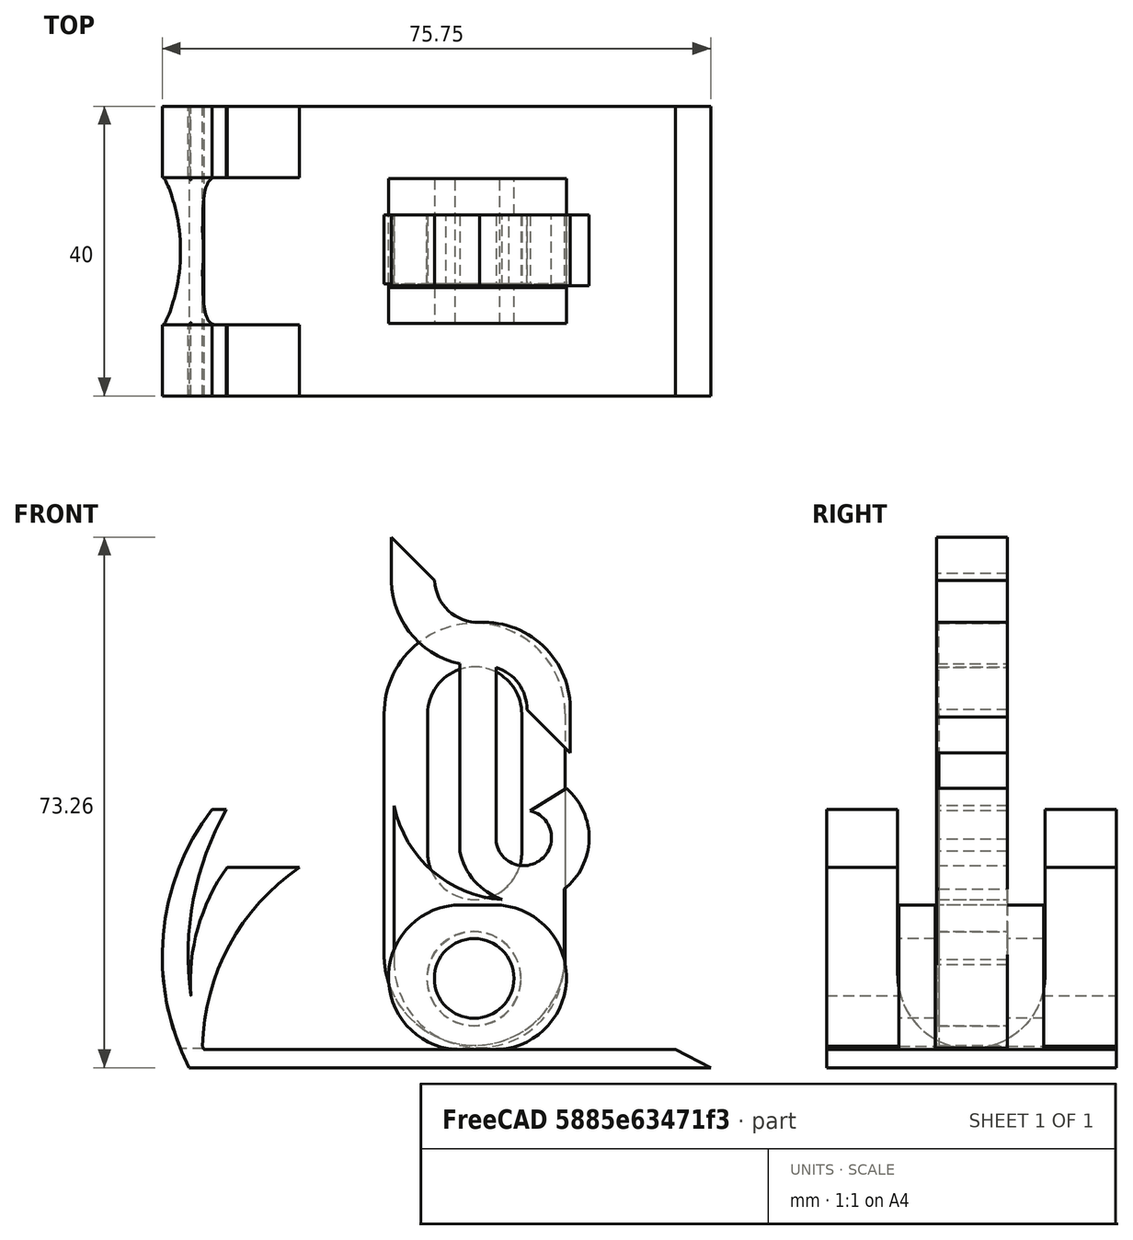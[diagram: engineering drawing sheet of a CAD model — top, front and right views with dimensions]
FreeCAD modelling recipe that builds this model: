
FCSTD DOCUMENT  (FreeCAD 0.16R6712 (Git))
Label: support_telephone4
License: All rights reserved
LicenseURL: http://en.wikipedia.org/wiki/All_rights_reserved
objects: Sketcher::SketchObject×10, PartDesign::Pad×9, App::DocumentObjectGroup×4, Part::Cut×2, Part::MultiFuse×2, PartDesign::Pocket×1, Mesh::Feature×1
note: 34 computed .brp shape members not serialized (recipe doc carries the construction recipe); baked Part::Feature solids carry a one-line shape summary decoded from their .brp

FEATURE [Sketcher::SketchObject] Sketch
  Placement = pos=(0,20,0) rot=(1,0,0;1.5708rad)
  sketch-geometry (10):
    g0: LineSegment StartX=-4.14304 StartY=-1.67863 StartZ=0 EndX=67.8914 EndY=-1.67863 EndZ=0
    g1: LineSegment StartX=-2.14304 StartY=0.821368 StartZ=0 EndX=63.0091 EndY=0.821368 EndZ=0
    g2: LineSegment StartX=63.0091 StartY=0.821368 StartZ=0 EndX=67.8914 EndY=-1.67863 EndZ=0
    g3: GeomPoint [constr] X=-1 Y=34 Z=0
    g4: GeomPoint [constr] X=1 Y=34 Z=0
    g5: ArcOfCircle CenterX=25.6862 CenterY=13.6714 CenterZ=0 NormalX=0 NormalY=0 NormalZ=1 Radius=33.5471 StartAngle=2.4906 EndAngle=3.61685
    g6: ArcOfCircle CenterX=36.4379 CenterY=13.9048 CenterZ=0 NormalX=0 NormalY=0 NormalZ=1 Radius=40.739 StartAngle=2.62575 EndAngle=3.46854
    g7: LineSegment StartX=-1 StartY=34 StartZ=0 EndX=1 EndY=34 EndZ=0
    g8: GeomPoint [constr] X=11 Y=26 Z=0
    g9: GeomPoint [constr] X=1.03178 Y=26 Z=0
  constraints (19):
    c: Horizontal(g0)
    c: Horizontal(g1)
    c: DistanceX(g0,g1) = 2
    c: Coincident(g2,g1)
    c: Coincident(g2,g0)
    c: DistanceX(g3,g-1) = 1
    c: DistanceY(g-1,g4) = 34
    c: DistanceY(g-1,g3) = 34
    c: DistanceX(g-1,g4) = 1
    c: Coincident(g5,g3)
    c: Coincident(g5,g0)
    c: Coincident(g6,g4)
    c: Coincident(g6,g1)
    c: Coincident(g7,g3)
    c: Coincident(g7,g4)
    c: DistanceY(g8,g4) = 8
    c: DistanceX(g4,g8) = 10
    c: DistanceY(g0,g1) = 2.5
    c: DistanceY(g-1,g1) = 0.821368
FEATURE [PartDesign::Pad] Pad
  Length = 40
  Length2 = 100
  Placement = pos=(0,20,0) rot=(1,0,0;1.5708rad)
  Sketch = -> Sketch
  Type = 0
FEATURE [Sketcher::SketchObject] Sketch001
  Placement = pos=(10,10,0) rot=(1,0,0;1.5708rad)
  sketch-geometry (4):
    g0: ArcOfCircle CenterX=23.3752 CenterY=10.7904 CenterZ=0 NormalX=0 NormalY=0 NormalZ=1 Radius=10 StartAngle=1.5708 EndAngle=4.71239
    g1: ArcOfCircle CenterX=27.9635 CenterY=10.7904 CenterZ=0 NormalX=0 NormalY=0 NormalZ=1 Radius=10 StartAngle=4.71239 EndAngle=7.85398
    g2: LineSegment StartX=23.3752 StartY=0.790424 StartZ=0 EndX=27.9635 EndY=0.790424 EndZ=0
    g3: LineSegment StartX=23.3752 StartY=20.7904 StartZ=0 EndX=27.9635 EndY=20.7904 EndZ=0
  constraints (7):
    c: Tangent(g0,g3) = 1.5708
    c: Tangent(g0,g2) = -1.5708
    c: Tangent(g2,g1) = -1.5708
    c: Tangent(g3,g1) = 1.5708
    c: Horizontal(g2)
    c: Equal(g0,g1)
    c: DistanceY(g1,g1) = 20
FEATURE [PartDesign::Pad] Pad001
  Length = 20
  Length2 = 100
  Placement = pos=(10,10,0) rot=(1,0,0;1.5708rad)
  Sketch = -> Sketch001
  Type = 0
FEATURE [Sketcher::SketchObject] Sketch002
  Placement = pos=(10,-10,0) rot=(1,0,0;1.5708rad)
  Support = -> Pad001 [Face6]
  sketch-geometry (1):
    g0: Circle CenterX=25.215 CenterY=10.6479 CenterZ=0 NormalX=0 NormalY=0 NormalZ=1 Radius=5.5
  constraints (1):
    c: Radius(g0) = 5.5
FEATURE [PartDesign::Pocket] Pocket
  Length = 24
  Placement = pos=(10,10,0) rot=(1,0,0;1.5708rad)
  Sketch = -> Sketch002
  Type = 0
FEATURE [Sketcher::SketchObject] Sketch003
  Placement = pos=(10,0,1) rot=(0,0,1;0rad)
  sketch-geometry (4):
    g0: LineSegment StartX=13.2912 StartY=5 StartZ=0 EndX=37.9673 EndY=5 EndZ=0
    g1: LineSegment StartX=37.9673 StartY=5 StartZ=0 EndX=37.9673 EndY=-5 EndZ=0
    g2: LineSegment StartX=37.9673 StartY=-5 StartZ=0 EndX=13.2912 EndY=-5 EndZ=0
    g3: LineSegment StartX=13.2912 StartY=-5 StartZ=0 EndX=13.2912 EndY=5 EndZ=0
  constraints (10):
    c: Coincident(g0,g1)
    c: Coincident(g1,g2)
    c: Coincident(g2,g3)
    c: Coincident(g3,g0)
    c: Horizontal(g0)
    c: Horizontal(g2)
    c: Vertical(g1)
    c: Vertical(g3)
    c: Symmetric(g0,g1,g-1)
    c: DistanceY(g1,g1) = 10
FEATURE [PartDesign::Pad] Pad002
  Length = 25
  Length2 = 100
  Placement = pos=(10,0,1) rot=(0,0,1;0rad)
  Sketch = -> Sketch003
  Type = 0
FEATURE [Part::Cut] Cut
  Base = -> Pocket
  Tool = -> Pad002
FEATURE [Sketcher::SketchObject] Sketch004
  Placement = pos=(10,5,0) rot=(1,0,0;1.5708rad)
  sketch-geometry (9):
    g0: ArcOfCircle CenterX=25.292 CenterY=47.1685 CenterZ=0 NormalX=0 NormalY=0 NormalZ=1 Radius=12.5141 StartAngle=0 EndAngle=3.14159
    g1: ArcOfCircle CenterX=25.292 CenterY=13.9216 CenterZ=0 NormalX=0 NormalY=0 NormalZ=1 Radius=12.5141 StartAngle=3.14159 EndAngle=6.28319
    g2: LineSegment StartX=12.7779 StartY=47.1685 StartZ=0 EndX=12.7779 EndY=13.9216 EndZ=0
    g3: LineSegment StartX=37.8061 StartY=47.1685 StartZ=0 EndX=37.8061 EndY=13.9216 EndZ=0
    g4: Circle CenterX=25.2029 CenterY=10.5785 CenterZ=0 NormalX=0 NormalY=0 NormalZ=1 Radius=6.5
    g5: ArcOfCircle CenterX=25.292 CenterY=47.1685 CenterZ=0 NormalX=0 NormalY=0 NormalZ=1 Radius=6.5 StartAngle=0 EndAngle=3.14159
    g6: ArcOfCircle CenterX=25.292 CenterY=28.0341 CenterZ=0 NormalX=0 NormalY=0 NormalZ=1 Radius=6.5 StartAngle=3.14159 EndAngle=6.28319
    g7: LineSegment StartX=18.792 StartY=47.1685 StartZ=0 EndX=18.792 EndY=28.0341 EndZ=0
    g8: LineSegment StartX=31.792 StartY=47.1685 StartZ=0 EndX=31.792 EndY=28.0341 EndZ=0
  constraints (15):
    c: Tangent(g0,g3) = 1.5708
    c: Tangent(g0,g2) = -1.5708
    c: Tangent(g2,g1) = -1.5708
    c: Tangent(g3,g1) = 1.5708
    c: Vertical(g2)
    c: Equal(g0,g1)
    c: Radius(g4) = 6.5
    c: Tangent(g5,g8) = 1.5708
    c: Tangent(g5,g7) = -1.5708
    c: Tangent(g7,g6) = -1.5708
    c: Tangent(g8,g6) = 1.5708
    c: Vertical(g7)
    c: Equal(g5,g6)
    c: Coincident(g5,g0)
    c: DistanceX(g5,g5) = 13
FEATURE [PartDesign::Pad] Pad003
  Length = 9.5
  Length2 = 100
  Placement = pos=(10,5,0) rot=(1,0,0;1.5708rad)
  Sketch = -> Sketch004
  Type = 0
FEATURE [App::DocumentObjectGroup] Groupe001  label="bielle"
  Group = -> [Pad003]
FEATURE [Sketcher::SketchObject] Sketch005
  Placement = pos=(0,5,0) rot=(1,0,0;1.5708rad)
  sketch-geometry (9):
    g0: ArcOfCircle CenterX=36.5044 CenterY=47.8329 CenterZ=0 NormalX=0 NormalY=0 NormalZ=1 Radius=6 StartAngle=6.27141 EndAngle=7.90556
    g1: ArcOfCircle CenterX=36.5044 CenterY=47.8329 CenterZ=0 NormalX=0 NormalY=0 NormalZ=1 Radius=12 StartAngle=6.19385 EndAngle=7.90026
    g2: ArcOfCircle CenterX=35.7669 CenterY=65.8173 CenterZ=0 NormalX=0 NormalY=0 NormalZ=1 Radius=6 StartAngle=3.18098 EndAngle=4.74278
    g3: ArcOfCircle CenterX=35.7669 CenterY=65.8173 CenterZ=0 NormalX=0 NormalY=0 NormalZ=1 Radius=12 StartAngle=3.0779 EndAngle=4.74808
    g4: GeomPoint [constr] X=35.7418 Y=56.8329 Z=0
    g5: LineSegment StartX=48.4566 StartY=46.7623 StartZ=0 EndX=48.4566 EndY=41.7623 EndZ=0
    g6: LineSegment StartX=42.504 StartY=47.7623 StartZ=0 EndX=48.4566 EndY=41.7623 EndZ=0
    g7: LineSegment StartX=23.7913 StartY=66.581 StartZ=0 EndX=23.7913 EndY=71.581 EndZ=0
    g8: LineSegment StartX=23.7913 StartY=71.581 StartZ=0 EndX=29.7716 EndY=65.581 EndZ=0
  constraints (23):
    c: Coincident(g1,g0)
    c: Radius(g1) = 12
    c: Radius(g0) = 6
    c: Coincident(g2,g1)
    c: Coincident(g3,g2)
    c: Coincident(g3,g0)
    c: Radius(g2) = 6
    c: Radius(g3) = 12
    c: DistanceX(g-1,g4) = 35.7418
    c: DistanceY(g-1,g4) = 56.8329
    c: DistanceY(g0,g4) = 9
    c: Coincident(g5,g1)
    c: Vertical(g5)
    c: Coincident(g6,g0)
    c: Coincident(g6,g5)
    c: DistanceY(g5,g5) = 5
    c: Coincident(g7,g3)
    c: Vertical(g7)
    c: Coincident(g8,g7)
    c: Coincident(g8,g2)
    c: DistanceY(g7,g7) = 5
    c: DistanceY(g2,g7) = 6
    c: DistanceY(g5,g0) = 6
FEATURE [Sketcher::SketchObject] Sketch006
  Placement = pos=(0,5,0) rot=(1,0,0;1.5708rad)
  sketch-geometry (6):
    g0: LineSegment StartX=33.2207 StartY=59.5118 StartZ=0 EndX=33.2207 EndY=28.1907 EndZ=0
    g1: LineSegment StartX=38.2207 StartY=59.3183 StartZ=0 EndX=38.2207 EndY=29.8591 EndZ=0
    g2: ArcOfCircle CenterX=42.054 CenterY=30.0624 CenterZ=0 NormalX=0 NormalY=0 NormalZ=1 Radius=9.02936 StartAngle=3.3504 EndAngle=7.14053
    g3: ArcOfCircle CenterX=42.054 CenterY=30.0624 CenterZ=0 NormalX=0 NormalY=0 NormalZ=1 Radius=3.83862 StartAngle=3.19457 EndAngle=7.61485
    g4: LineSegment StartX=42.9632 StartY=33.7918 StartZ=0 EndX=47.9632 EndY=36.8896 EndZ=0
    g5: LineSegment StartX=33.2207 StartY=59.5118 StartZ=0 EndX=38.2207 EndY=59.3183 EndZ=0
  constraints (11):
    c: Vertical(g0)
    c: Vertical(g1)
    c: DistanceX(g0,g1) = 5
    c: Coincident(g2,g0)
    c: Coincident(g3,g2)
    c: Coincident(g3,g1)
    c: Coincident(g4,g3)
    c: Coincident(g4,g2)
    c: DistanceX(g3,g2) = 5
    c: Coincident(g5,g0)
    c: Coincident(g5,g1)
FEATURE [Sketcher::SketchObject] Sketch007
  Placement = pos=(0,5,0) rot=(1,0,0;1.5708rad)
  sketch-geometry (5):
    g0: Circle CenterX=35.1655 CenterY=10.6403 CenterZ=0 NormalX=0 NormalY=0 NormalZ=1 Radius=6.5
    g1: ArcOfCircle CenterX=35.9044 CenterY=12.8543 CenterZ=0 NormalX=0 NormalY=0 NormalZ=1 Radius=11.7583 StartAngle=3.10975 EndAngle=6.25328
    g2: LineSegment StartX=47.6574 StartY=12.5027 StartZ=0 EndX=47.6574 EndY=23.355 EndZ=0
    g3: LineSegment StartX=24.1521 StartY=34.4704 StartZ=0 EndX=24.1521 EndY=13.2287 EndZ=0
    g4: ArcOfCircle CenterX=40.1211 CenterY=37.8289 CenterZ=0 NormalX=0 NormalY=0 NormalZ=1 Radius=16.3184 StartAngle=3.34889 EndAngle=5.19244
  constraints (7):
    c: Radius(g0) = 6.5
    c: Coincident(g2,g1)
    c: Vertical(g2)
    c: Coincident(g3,g1)
    c: Vertical(g3)
    c: Coincident(g4,g3)
    c: Coincident(g4,g2)
FEATURE [PartDesign::Pad] Pad004
  Length = 9.8
  Length2 = 100
  Placement = pos=(0,5,0) rot=(1,0,0;1.5708rad)
  Sketch = -> Sketch006
  Type = 0
FEATURE [PartDesign::Pad] Pad005
  Length = 9.8
  Length2 = 100
  Placement = pos=(0,5,0) rot=(1,0,0;1.5708rad)
  Sketch = -> Sketch005
  Type = 0
FEATURE [PartDesign::Pad] Pad006
  Length = 9.8
  Length2 = 100
  Placement = pos=(0,5,0) rot=(1,0,0;1.5708rad)
  Sketch = -> Sketch007
  Type = 0
FEATURE [Part::MultiFuse] Fusion
  Shapes = -> [Pad004,Pad005,Pad006]
FEATURE [App::DocumentObjectGroup] Groupe002  label="bielle_J"
  Group = -> [Fusion]
FEATURE [Sketcher::SketchObject] Sketch008
  Placement = pos=(0,20,0) rot=(1,0,0;1.5708rad)
  sketch-geometry (6):
    g0: GeomPoint [constr] X=11.0569 Y=25.9534 Z=0
    g1: GeomPoint [constr] X=1.09392 Y=25.9534 Z=0
    g2: GeomPoint [constr] X=-2.3075 Y=0.868989 Z=0
    g3: ArcOfCircle CenterX=28.3339 CenterY=0.646249 CenterZ=0 NormalX=0 NormalY=0 NormalZ=1 Radius=30.6423 StartAngle=2.16981 EndAngle=3.13432
    g4: ArcOfCircle CenterX=22.9513 CenterY=10.2167 CenterZ=0 NormalX=0 NormalY=0 NormalZ=1 Radius=26.933 StartAngle=2.51759 EndAngle=3.49604
    g5: LineSegment StartX=1.09392 StartY=25.9534 StartZ=0 EndX=11.0569 EndY=25.9534 EndZ=0
  constraints (7):
    c: Coincident(g3,g0)
    c: Coincident(g3,g2)
    c: Coincident(g4,g1)
    c: Coincident(g4,g2)
    c: Coincident(g5,g1)
    c: Coincident(g5,g0)
    c: Horizontal(g5)
FEATURE [PartDesign::Pad] Pad007
  Length = 40
  Length2 = 100
  Placement = pos=(0,20,0) rot=(1,0,0;1.5708rad)
  Sketch = -> Sketch008
  Type = 0
FEATURE [Sketcher::SketchObject] Sketch009
  Placement = pos=(-17,0,0) rot=(0.57735,0.57735,0.57735;2.0944rad)
  sketch-geometry (4):
    g0: ArcOfCircle CenterX=0 CenterY=61.1287 CenterZ=0 NormalX=0 NormalY=0 NormalZ=1 Radius=10.1729 StartAngle=0 EndAngle=3.14159
    g1: ArcOfCircle CenterX=0 CenterY=11.1287 CenterZ=0 NormalX=0 NormalY=0 NormalZ=1 Radius=10.1729 StartAngle=3.14159 EndAngle=6.28319
    g2: LineSegment StartX=-10.1729 StartY=61.1287 StartZ=0 EndX=-10.1729 EndY=11.1287 EndZ=0
    g3: LineSegment StartX=10.1729 StartY=61.1287 StartZ=0 EndX=10.1729 EndY=11.1287 EndZ=0
  constraints (8):
    c: Tangent(g0,g3) = 1.5708
    c: Tangent(g0,g2) = -1.5708
    c: Tangent(g2,g1) = -1.5708
    c: Tangent(g3,g1) = 1.5708
    c: Vertical(g2)
    c: Equal(g0,g1)
    c: PointOnObject(g0,g-2)
    c: DistanceY(g3,g3) = 50
FEATURE [PartDesign::Pad] Pad008
  Length = 30
  Length2 = 100
  Placement = pos=(-17,0,0) rot=(0.57735,0.57735,0.57735;2.0944rad)
  Sketch = -> Sketch009
  Type = 0
FEATURE [Part::MultiFuse] Fusion001
  Shapes = -> [Pad,Cut,Pad007]
FEATURE [Part::Cut] Cut001
  Base = -> Fusion001
  Tool = -> Pad008
FEATURE [App::DocumentObjectGroup] Groupe  label="corp"
  Group = -> [Pad001,Cut001]
FEATURE [Mesh::Feature] vis_ecrou
  Placement = pos=(-52,0,-3) rot=(0,0,1;0rad)
FEATURE [App::DocumentObjectGroup] Groupe003  label="vis_ecrou001"
  Group = -> [vis_ecrou]
